annotation { "Feature Type Name" : "Feature", "Feature Type Description" : "" }
export const myFeature = defineFeature(function(context is Context, id is Id, definition is map)
    precondition{}
    {
        {
            var Q0;
            Q0=qCreatedBy(makeId("Top.planeOp"),FACE);
            var sketch = newSketch(context, id + "F0", { "sketchPlane" : qUnion([Q0])});
            skLineSegment(sketch, "E0.bottom", {"start": v(0, 0) * mm, "end": v(300, 0) * mm});
            skLineSegment(sketch, "E0.top", {"start": v(0, 148) * mm, "end": v(300, 148) * mm});
            skLineSegment(sketch, "E0.left", {"start": v(0, 0) * mm, "end": v(0, 148) * mm});
            skLineSegment(sketch, "E0.right", {"start": v(300, 0) * mm, "end": v(300, 148) * mm});
            skLineSegment(sketch, "E1.0", {"start": v(5, 143) * mm, "end": v(295, 143) * mm});
            skLineSegment(sketch, "E1.1", {"start": v(5, 5) * mm, "end": v(5, 143) * mm});
            skLineSegment(sketch, "E1.2", {"start": v(5, 5) * mm, "end": v(295, 5) * mm});
            skLineSegment(sketch, "E1.3", {"start": v(295, 5) * mm, "end": v(295, 143) * mm});
            skSolve(sketch);
        }
        {
            var Q0;
            Q0=qCreatedBy(makeId("Top.planeOp"),FACE);
            var sketch = newSketch(context, id + "F1", { "sketchPlane" : qUnion([Q0])});
            skLineSegment(sketch, "E2.bottom", {"start": v(159.6, 227.06) * mm, "end": v(245.86, 227.06) * mm});
            skLineSegment(sketch, "E2.top", {"start": v(159.6, 250.42) * mm, "end": v(245.86, 250.42) * mm});
            skLineSegment(sketch, "E2.left", {"start": v(159.6, 227.06) * mm, "end": v(159.6, 250.42) * mm});
            skLineSegment(sketch, "E2.right", {"start": v(245.86, 227.06) * mm, "end": v(245.86, 250.42) * mm});
            skLineSegment(sketch, "E3.bottom", {"start": v(5, 143) * mm, "end": v(295, 143) * mm, "construction": true});
            skLineSegment(sketch, "E3.top", {"start": v(5, 5) * mm, "end": v(295, 5) * mm, "construction": true});
            skLineSegment(sketch, "E3.left", {"start": v(5, 143) * mm, "end": v(5, 5) * mm, "construction": true});
            skLineSegment(sketch, "E3.right", {"start": v(295, 143) * mm, "end": v(295, 5) * mm, "construction": true});
            skLineSegment(sketch, "E4", {"start": v(5, 95) * mm, "end": v(295, 95) * mm, "construction": true});
            skLineSegment(sketch, "E5", {"start": v(5, 55) * mm, "end": v(295, 55) * mm, "construction": true});
            skLineSegment(sketch, "E6", {"start": v(5, 130) * mm, "end": v(295, 130) * mm, "construction": true});
            skLineSegment(sketch, "E7", {"start": v(5, 27) * mm, "end": v(295, 27) * mm, "construction": true});
            skLineSegment(sketch, "E8", {"start": v(5, 42) * mm, "end": v(295, 42) * mm, "construction": true});
            skLineSegment(sketch, "E9", {"start": v(295, 68) * mm, "end": v(5, 68) * mm, "construction": true});
            skSolve(sketch);
        }
        {
            var Q0;
            Q0=qCreatedBy(makeId("Top.planeOp"),FACE);
            var sketch = newSketch(context, id + "F2", { "sketchPlane" : qUnion([Q0])});
            skCircle(sketch, "E10", {"center": v(100, 130) * mm, "radius": 5 * mm});
            skCircle(sketch, "E11.1.0.0", {"center": v(125, 130) * mm, "radius": 5 * mm});
            skCircle(sketch, "E11.2.0.0", {"center": v(150, 130) * mm, "radius": 5 * mm});
            skCircle(sketch, "E11.3.0.0", {"center": v(175, 130) * mm, "radius": 5 * mm});
            skCircle(sketch, "E11.4.0.0", {"center": v(200, 130) * mm, "radius": 5 * mm});
            skCircle(sketch, "E11.5.0.0", {"center": v(225, 130) * mm, "radius": 5 * mm});
            skLineSegment(sketch, "E11.direction1", {"start": v(100, 130) * mm, "end": v(125, 130) * mm, "construction": true});
            skSolve(sketch);
        }
        {
            var Q0;
            Q0=qCreatedBy(makeId("Top.planeOp"),FACE);
            var sketch = newSketch(context, id + "F3", { "sketchPlane" : qUnion([Q0])});
            skCircle(sketch, "E12", {"center": v(35, 95) * mm, "radius": 15 * mm});
            skCircle(sketch, "E13.1.0.0", {"center": v(85, 95) * mm, "radius": 15 * mm});
            skCircle(sketch, "E13.2.0.0", {"center": v(135, 95) * mm, "radius": 15 * mm});
            skLineSegment(sketch, "E13.direction1", {"start": v(35, 95) * mm, "end": v(85, 95) * mm, "construction": true});
            skCircle(sketch, "E14", {"center": v(250, 95) * mm, "radius": 15 * mm});
            skSolve(sketch);
        }
        {
            var Q0;
            Q0=qCreatedBy(makeId("Top.planeOp"),FACE);
            var sketch = newSketch(context, id + "F4", { "sketchPlane" : qUnion([Q0])});
            skLineSegment(sketch, "E15.bottom", {"start": v(67.5, 35) * mm, "end": v(62.5, 35) * mm});
            skLineSegment(sketch, "E15.top", {"start": v(67.5, 19) * mm, "end": v(62.5, 19) * mm});
            skLineSegment(sketch, "E15.left", {"start": v(67.5, 35) * mm, "end": v(67.5, 19) * mm});
            skLineSegment(sketch, "E15.right", {"start": v(62.5, 35) * mm, "end": v(62.5, 19) * mm});
            skPoint(sketch, "E15.middle", {"position": v(65, 27) * mm});
            skLineSegment(sketch, "E16.1.0.0", {"start": v(78.5, 35) * mm, "end": v(78.5, 19) * mm});
            skLineSegment(sketch, "E16.1.0.1", {"start": v(83.5, 35) * mm, "end": v(78.5, 35) * mm});
            skLineSegment(sketch, "E16.1.0.2", {"start": v(83.5, 19) * mm, "end": v(78.5, 19) * mm});
            skLineSegment(sketch, "E16.1.0.3", {"start": v(83.5, 35) * mm, "end": v(83.5, 19) * mm});
            skLineSegment(sketch, "E16.2.0.0", {"start": v(94.5, 35) * mm, "end": v(94.5, 19) * mm});
            skLineSegment(sketch, "E16.2.0.1", {"start": v(99.5, 35) * mm, "end": v(94.5, 35) * mm});
            skLineSegment(sketch, "E16.2.0.2", {"start": v(99.5, 19) * mm, "end": v(94.5, 19) * mm});
            skLineSegment(sketch, "E16.2.0.3", {"start": v(99.5, 35) * mm, "end": v(99.5, 19) * mm});
            skLineSegment(sketch, "E16.3.0.0", {"start": v(110.5, 35) * mm, "end": v(110.5, 19) * mm});
            skLineSegment(sketch, "E16.3.0.1", {"start": v(115.5, 35) * mm, "end": v(110.5, 35) * mm});
            skLineSegment(sketch, "E16.3.0.2", {"start": v(115.5, 19) * mm, "end": v(110.5, 19) * mm});
            skLineSegment(sketch, "E16.3.0.3", {"start": v(115.5, 35) * mm, "end": v(115.5, 19) * mm});
            skLineSegment(sketch, "E16.4.0.0", {"start": v(126.5, 35) * mm, "end": v(126.5, 19) * mm});
            skLineSegment(sketch, "E16.4.0.1", {"start": v(131.5, 35) * mm, "end": v(126.5, 35) * mm});
            skLineSegment(sketch, "E16.4.0.2", {"start": v(131.5, 19) * mm, "end": v(126.5, 19) * mm});
            skLineSegment(sketch, "E16.4.0.3", {"start": v(131.5, 35) * mm, "end": v(131.5, 19) * mm});
            skLineSegment(sketch, "E16.5.0.0", {"start": v(142.5, 35) * mm, "end": v(142.5, 19) * mm});
            skLineSegment(sketch, "E16.5.0.1", {"start": v(147.5, 35) * mm, "end": v(142.5, 35) * mm});
            skLineSegment(sketch, "E16.5.0.2", {"start": v(147.5, 19) * mm, "end": v(142.5, 19) * mm});
            skLineSegment(sketch, "E16.5.0.3", {"start": v(147.5, 35) * mm, "end": v(147.5, 19) * mm});
            skLineSegment(sketch, "E16.6.0.0", {"start": v(158.5, 35) * mm, "end": v(158.5, 19) * mm});
            skLineSegment(sketch, "E16.6.0.1", {"start": v(163.5, 35) * mm, "end": v(158.5, 35) * mm});
            skLineSegment(sketch, "E16.6.0.2", {"start": v(163.5, 19) * mm, "end": v(158.5, 19) * mm});
            skLineSegment(sketch, "E16.6.0.3", {"start": v(163.5, 35) * mm, "end": v(163.5, 19) * mm});
            skLineSegment(sketch, "E16.7.0.0", {"start": v(174.5, 35) * mm, "end": v(174.5, 19) * mm});
            skLineSegment(sketch, "E16.7.0.1", {"start": v(179.5, 35) * mm, "end": v(174.5, 35) * mm});
            skLineSegment(sketch, "E16.7.0.2", {"start": v(179.5, 19) * mm, "end": v(174.5, 19) * mm});
            skLineSegment(sketch, "E16.7.0.3", {"start": v(179.5, 35) * mm, "end": v(179.5, 19) * mm});
            skLineSegment(sketch, "E16.8.0.0", {"start": v(190.5, 35) * mm, "end": v(190.5, 19) * mm});
            skLineSegment(sketch, "E16.8.0.1", {"start": v(195.5, 35) * mm, "end": v(190.5, 35) * mm});
            skLineSegment(sketch, "E16.8.0.2", {"start": v(195.5, 19) * mm, "end": v(190.5, 19) * mm});
            skLineSegment(sketch, "E16.8.0.3", {"start": v(195.5, 35) * mm, "end": v(195.5, 19) * mm});
            skLineSegment(sketch, "E16.9.0.0", {"start": v(206.5, 35) * mm, "end": v(206.5, 19) * mm});
            skLineSegment(sketch, "E16.9.0.1", {"start": v(211.5, 35) * mm, "end": v(206.5, 35) * mm});
            skLineSegment(sketch, "E16.9.0.2", {"start": v(211.5, 19) * mm, "end": v(206.5, 19) * mm});
            skLineSegment(sketch, "E16.9.0.3", {"start": v(211.5, 35) * mm, "end": v(211.5, 19) * mm});
            skLineSegment(sketch, "E16.direction1", {"start": v(62.5, 19) * mm, "end": v(78.5, 19) * mm, "construction": true});
            skLineSegment(sketch, "E17.0.10.0", {"start": v(222.5, 35) * mm, "end": v(222.5, 19) * mm});
            skLineSegment(sketch, "E17.3.10.0", {"start": v(227.5, 35) * mm, "end": v(222.5, 35) * mm});
            skLineSegment(sketch, "E17.6.10.0", {"start": v(227.5, 19) * mm, "end": v(222.5, 19) * mm});
            skLineSegment(sketch, "E17.9.10.0", {"start": v(227.5, 35) * mm, "end": v(227.5, 19) * mm});
            skLineSegment(sketch, "E17.0.11.0", {"start": v(238.5, 35) * mm, "end": v(238.5, 19) * mm});
            skLineSegment(sketch, "E17.3.11.0", {"start": v(243.5, 35) * mm, "end": v(238.5, 35) * mm});
            skLineSegment(sketch, "E17.6.11.0", {"start": v(243.5, 19) * mm, "end": v(238.5, 19) * mm});
            skLineSegment(sketch, "E17.9.11.0", {"start": v(243.5, 35) * mm, "end": v(243.5, 19) * mm});
            skLineSegment(sketch, "E18.bottom", {"start": v(124.5, 63) * mm, "end": v(119.5, 63) * mm});
            skLineSegment(sketch, "E18.top", {"start": v(124.5, 47) * mm, "end": v(119.5, 47) * mm});
            skLineSegment(sketch, "E18.left", {"start": v(124.5, 63) * mm, "end": v(124.5, 47) * mm});
            skLineSegment(sketch, "E18.right", {"start": v(119.5, 63) * mm, "end": v(119.5, 47) * mm});
            skPoint(sketch, "E18.middle", {"position": v(122, 55) * mm});
            skLineSegment(sketch, "E19.bottom", {"start": v(156.5, 63) * mm, "end": v(151.5, 63) * mm});
            skLineSegment(sketch, "E19.top", {"start": v(156.5, 47) * mm, "end": v(151.5, 47) * mm});
            skLineSegment(sketch, "E19.left", {"start": v(156.5, 63) * mm, "end": v(156.5, 47) * mm});
            skLineSegment(sketch, "E19.right", {"start": v(151.5, 63) * mm, "end": v(151.5, 47) * mm});
            skPoint(sketch, "E19.middle", {"position": v(154, 55) * mm});
            skLineSegment(sketch, "E20.bottom", {"start": v(140.5, 63) * mm, "end": v(135.5, 63) * mm});
            skLineSegment(sketch, "E20.top", {"start": v(140.5, 47) * mm, "end": v(135.5, 47) * mm});
            skLineSegment(sketch, "E20.left", {"start": v(140.5, 63) * mm, "end": v(140.5, 47) * mm});
            skLineSegment(sketch, "E20.right", {"start": v(135.5, 63) * mm, "end": v(135.5, 47) * mm});
            skPoint(sketch, "E20.middle", {"position": v(138, 55) * mm});
            skLineSegment(sketch, "E21.bottom", {"start": v(92.5, 63) * mm, "end": v(87.5, 63) * mm});
            skLineSegment(sketch, "E21.top", {"start": v(92.5, 47) * mm, "end": v(87.5, 47) * mm});
            skLineSegment(sketch, "E21.left", {"start": v(92.5, 63) * mm, "end": v(92.5, 47) * mm});
            skLineSegment(sketch, "E21.right", {"start": v(87.5, 63) * mm, "end": v(87.5, 47) * mm});
            skPoint(sketch, "E21.middle", {"position": v(90, 55) * mm});
            skLineSegment(sketch, "E22.bottom", {"start": v(76.5, 63) * mm, "end": v(71.5, 63) * mm});
            skLineSegment(sketch, "E22.top", {"start": v(76.5, 47) * mm, "end": v(71.5, 47) * mm});
            skLineSegment(sketch, "E22.left", {"start": v(76.5, 63) * mm, "end": v(76.5, 47) * mm});
            skLineSegment(sketch, "E22.right", {"start": v(71.5, 63) * mm, "end": v(71.5, 47) * mm});
            skPoint(sketch, "E22.middle", {"position": v(74, 55) * mm});
            skPoint(sketch, "E23", {"position": v(76.5, 55) * mm});
            skLineSegment(sketch, "E24.bottom", {"start": v(249, 57.5) * mm, "end": v(233, 57.5) * mm});
            skLineSegment(sketch, "E24.top", {"start": v(249, 52.5) * mm, "end": v(233, 52.5) * mm});
            skLineSegment(sketch, "E24.left", {"start": v(249, 57.5) * mm, "end": v(249, 52.5) * mm});
            skLineSegment(sketch, "E24.right", {"start": v(233, 57.5) * mm, "end": v(233, 52.5) * mm});
            skPoint(sketch, "E24.middle", {"position": v(241, 55) * mm});
            skLineSegment(sketch, "E25.bottom", {"start": v(283, 19) * mm, "end": v(263, 19) * mm});
            skLineSegment(sketch, "E25.top", {"start": v(283, 35) * mm, "end": v(263, 35) * mm});
            skLineSegment(sketch, "E25.left", {"start": v(283, 19) * mm, "end": v(283, 35) * mm});
            skLineSegment(sketch, "E25.right", {"start": v(263, 19) * mm, "end": v(263, 35) * mm});
            skPoint(sketch, "E25.middle", {"position": v(273, 27) * mm});
            skLineSegment(sketch, "E26.bottom", {"start": v(35, 19) * mm, "end": v(15, 19) * mm});
            skLineSegment(sketch, "E26.top", {"start": v(35, 35) * mm, "end": v(15, 35) * mm});
            skLineSegment(sketch, "E26.left", {"start": v(35, 19) * mm, "end": v(35, 35) * mm});
            skLineSegment(sketch, "E26.right", {"start": v(15, 19) * mm, "end": v(15, 35) * mm});
            skPoint(sketch, "E26.middle", {"position": v(25, 27) * mm});
            skPoint(sketch, "E27", {"position": v(83.5, 27) * mm});
            skPoint(sketch, "E28", {"position": v(241, 35) * mm});
            skLineSegment(sketch, "E29.bottom", {"start": v(281, 60) * mm, "end": v(265, 60) * mm});
            skLineSegment(sketch, "E29.top", {"start": v(281, 55) * mm, "end": v(265, 55) * mm});
            skLineSegment(sketch, "E29.left", {"start": v(281, 60) * mm, "end": v(281, 55) * mm});
            skLineSegment(sketch, "E29.right", {"start": v(265, 60) * mm, "end": v(265, 55) * mm});
            skPoint(sketch, "E29.middle", {"position": v(273, 57.5) * mm});
            skPoint(sketch, "E30", {"position": v(273, 35) * mm});
            skLineSegment(sketch, "E31.bottom", {"start": v(33, 57.5) * mm, "end": v(17, 57.5) * mm});
            skLineSegment(sketch, "E31.top", {"start": v(33, 52.5) * mm, "end": v(17, 52.5) * mm});
            skLineSegment(sketch, "E31.left", {"start": v(33, 57.5) * mm, "end": v(33, 52.5) * mm});
            skLineSegment(sketch, "E31.right", {"start": v(17, 57.5) * mm, "end": v(17, 52.5) * mm});
            skPoint(sketch, "E31.middle", {"position": v(25, 55) * mm});
            skLineSegment(sketch, "E32.bottom", {"start": v(47.5, 19) * mm, "end": v(42.5, 19) * mm});
            skLineSegment(sketch, "E32.top", {"start": v(47.5, 35) * mm, "end": v(42.5, 35) * mm});
            skLineSegment(sketch, "E32.left", {"start": v(47.5, 19) * mm, "end": v(47.5, 35) * mm});
            skLineSegment(sketch, "E32.right", {"start": v(42.5, 19) * mm, "end": v(42.5, 35) * mm});
            skPoint(sketch, "E32.middle", {"position": v(45, 27) * mm});
            skCircle(sketch, "E33", {"center": v(145, 42) * mm, "radius": 1.5 * mm});
            skCircle(sketch, "E34", {"center": v(161, 42) * mm, "radius": 1.5 * mm});
            skCircle(sketch, "E35", {"center": v(129, 42) * mm, "radius": 1.5 * mm});
            skCircle(sketch, "E36", {"center": v(113, 42) * mm, "radius": 1.5 * mm});
            skCircle(sketch, "E37", {"center": v(74, 68) * mm, "radius": 1.5 * mm});
            skCircle(sketch, "E38", {"center": v(90, 68) * mm, "radius": 1.5 * mm});
            skCircle(sketch, "E39", {"center": v(97, 42) * mm, "radius": 1.5 * mm});
            skCircle(sketch, "E40", {"center": v(81, 42) * mm, "radius": 1.5 * mm});
            skCircle(sketch, "E41", {"center": v(65, 42) * mm, "radius": 1.5 * mm});
            skPoint(sketch, "E42", {"position": v(65, 35) * mm});
            skPoint(sketch, "E43", {"position": v(81, 35) * mm});
            skPoint(sketch, "E44", {"position": v(97, 35) * mm});
            skPoint(sketch, "E45", {"position": v(113, 35) * mm});
            skPoint(sketch, "E46", {"position": v(129, 35) * mm});
            skPoint(sketch, "E47", {"position": v(145, 35) * mm});
            skPoint(sketch, "E48", {"position": v(161, 35) * mm});
            skCircle(sketch, "E49", {"center": v(209, 42) * mm, "radius": 1.5 * mm});
            skCircle(sketch, "E50", {"center": v(225, 42) * mm, "radius": 1.5 * mm});
            skCircle(sketch, "E51", {"center": v(154, 68) * mm, "radius": 1.5 * mm});
            skCircle(sketch, "E52", {"center": v(138, 68) * mm, "radius": 1.5 * mm});
            skCircle(sketch, "E53", {"center": v(217, 68) * mm, "radius": 1.5 * mm});
            skCircle(sketch, "E54", {"center": v(122, 68) * mm, "radius": 1.5 * mm});
            skCircle(sketch, "E55", {"center": v(177, 42) * mm, "radius": 1.5 * mm});
            skCircle(sketch, "E56", {"center": v(193, 42) * mm, "radius": 1.5 * mm});
            skPoint(sketch, "E57", {"position": v(122, 63) * mm});
            skPoint(sketch, "E58", {"position": v(138, 63) * mm});
            skPoint(sketch, "E59", {"position": v(154, 63) * mm});
            skPoint(sketch, "E60", {"position": v(177, 35) * mm});
            skPoint(sketch, "E61", {"position": v(193, 35) * mm});
            skPoint(sketch, "E62", {"position": v(209, 35) * mm});
            skPoint(sketch, "E63", {"position": v(225, 35) * mm});
            skCircle(sketch, "E64", {"center": v(25, 42) * mm, "radius": 1.5 * mm});
            skPoint(sketch, "E65", {"position": v(25, 35) * mm});
            skLineSegment(sketch, "E66.bottom", {"start": v(47.5, 52.5) * mm, "end": v(63.5, 52.5) * mm});
            skLineSegment(sketch, "E66.top", {"start": v(47.5, 57.5) * mm, "end": v(63.5, 57.5) * mm});
            skLineSegment(sketch, "E66.left", {"start": v(47.5, 52.5) * mm, "end": v(47.5, 57.5) * mm});
            skLineSegment(sketch, "E66.right", {"start": v(63.5, 52.5) * mm, "end": v(63.5, 57.5) * mm});
            skCircle(sketch, "E67", {"center": v(55.5, 68) * mm, "radius": 1.5 * mm});
            skPoint(sketch, "E67.centerSnap0", {"position": v(55.5, 57.5) * mm});
            skSolve(sketch);
        }
        {
            var Q0;
            Q0=qCreatedBy(makeId("Top.planeOp"),FACE);
            var sketch = newSketch(context, id + "F5", { "sketchPlane" : qUnion([Q0])});
            skText(sketch, "E68", { "text": "TB 303", "fontName": "OpenSans-Regular.ttf"});
            skPoint(sketch, "E69", {"position": v(197.71, 95) * mm});
            skText(sketch, "E70", { "text": "Compueter Controled\n", "fontName": "OpenSans-Regular.ttf"});
            skLineSegment(sketch, "E71", {"start": v(215.4, 87) * mm, "end": v(215.4, 91) * mm, "construction": true});
            skText(sketch, "E72", { "text": "Roland", "fontName": "OpenSans-Regular.ttf"});
            skText(sketch, "E73", { "text": "Bass line", "fontName": "OpenSans-Regular.ttf"});
            const initialGuessF5  = {"E68": [0.18003, 0.091, 1, 0, 0.008], "E70": [0.15897, 0.083, 1, 0, 0.004], "E72": [0.029, 0.124, 1, 0, 0.01], "E73": [0.23932, 0.124, 1, 0, 0.008]};
            skSetInitialGuess(sketch, initialGuessF5);
            skSolve(sketch);
        }
        {
            var Q0;
            Q0=makeQuery(id+"F0.imprint","IMPRINT",FACE,{"disambiguationData":[TD([[makeQuery(id+"F0.imprint","IMPRINT",EDGE,{"derivedFrom":sQuery(id+"F0.wireOp",EDGE,"E1.0")}),-1.0]])]});
            extrude(context, id + "F6", {"entities" : qUnion([Q0]), "depth" : 55 * mm, "hasSecondDirection" : true, "secondDirectionOppositeDirection" : false, "secondDirectionDepth" : 50 * mm});
        }
        {
            var Q0;
            Q0=makeQuery(id+"F4.imprint","IMPRINT",FACE,{"disambiguationData":[TD([[makeQuery(id+"F4.imprint","IMPRINT",EDGE,{"derivedFrom":sQuery(id+"F4.wireOp",EDGE,"E16.6.0.0")}),1.0]])]});
            var Q1;
            Q1=makeQuery(id+"F4.imprint","IMPRINT",FACE,{"disambiguationData":[TD([[makeQuery(id+"F4.imprint","IMPRINT",EDGE,{"derivedFrom":sQuery(id+"F4.wireOp",EDGE,"E16.2.0.0")}),1.0]])]});
            var Q2;
            Q2=makeQuery(id+"F4.imprint","IMPRINT",FACE,{"disambiguationData":[TD([[makeQuery(id+"F4.imprint","IMPRINT",EDGE,{"derivedFrom":sQuery(id+"F4.wireOp",EDGE,"E17.0.11.0")}),1.0]])]});
            var Q3;
            Q3=makeQuery(id+"F4.imprint","IMPRINT",FACE,{"disambiguationData":[TD([[makeQuery(id+"F4.imprint","IMPRINT",EDGE,{"derivedFrom":sQuery(id+"F4.wireOp",EDGE,"E16.4.0.0")}),1.0]])]});
            var Q4;
            Q4=makeQuery(id+"F3.imprint","IMPRINT",FACE,{"disambiguationData":[TD([[makeQuery(id+"F3.imprint","IMPRINT",EDGE,{"derivedFrom":sQuery(id+"F3.wireOp",EDGE,"E14")}),1.0]])]});
            var Q5;
            Q5=makeQuery(id+"F4.imprint","IMPRINT",FACE,{"disambiguationData":[TD([[makeQuery(id+"F4.imprint","IMPRINT",EDGE,{"derivedFrom":sQuery(id+"F4.wireOp",EDGE,"E16.3.0.0")}),1.0]])]});
            var Q6;
            Q6=makeQuery(id+"F4.imprint","IMPRINT",FACE,{"disambiguationData":[TD([[makeQuery(id+"F4.imprint","IMPRINT",EDGE,{"derivedFrom":sQuery(id+"F4.wireOp",EDGE,"E16.5.0.0")}),1.0]])]});
            var Q7;
            Q7=makeQuery(id+"F4.imprint","IMPRINT",FACE,{"disambiguationData":[TD([[makeQuery(id+"F4.imprint","IMPRINT",EDGE,{"derivedFrom":sQuery(id+"F4.wireOp",EDGE,"E16.7.0.0")}),1.0]])]});
            var Q8;
            Q8=makeQuery(id+"F3.imprint","IMPRINT",FACE,{"disambiguationData":[TD([[makeQuery(id+"F3.imprint","IMPRINT",EDGE,{"derivedFrom":sQuery(id+"F3.wireOp",EDGE,"E13.1.0.0")}),1.0]])]});
            var Q9;
            Q9=makeQuery(id+"F4.imprint","IMPRINT",FACE,{"disambiguationData":[TD([[makeQuery(id+"F4.imprint","IMPRINT",EDGE,{"derivedFrom":sQuery(id+"F4.wireOp",EDGE,"E17.0.10.0")}),1.0]])]});
            var Q10;
            Q10=makeQuery(id+"F4.imprint","IMPRINT",FACE,{"disambiguationData":[TD([[makeQuery(id+"F4.imprint","IMPRINT",EDGE,{"derivedFrom":sQuery(id+"F4.wireOp",EDGE,"E26.bottom")}),-1.0]])]});
            var Q11;
            Q11=makeQuery(id+"F4.imprint","IMPRINT",FACE,{"disambiguationData":[TD([[makeQuery(id+"F4.imprint","IMPRINT",EDGE,{"derivedFrom":sQuery(id+"F4.wireOp",EDGE,"E25.bottom")}),-1.0]])]});
            var Q12;
            Q12=makeQuery(id+"F3.imprint","IMPRINT",FACE,{"disambiguationData":[TD([[makeQuery(id+"F3.imprint","IMPRINT",EDGE,{"derivedFrom":sQuery(id+"F3.wireOp",EDGE,"E12")}),1.0]])]});
            var Q13;
            Q13=makeQuery(id+"F4.imprint","IMPRINT",FACE,{"disambiguationData":[TD([[makeQuery(id+"F4.imprint","IMPRINT",EDGE,{"derivedFrom":sQuery(id+"F4.wireOp",EDGE,"E16.9.0.0")}),1.0]])]});
            var Q14;
            Q14=makeQuery(id+"F3.imprint","IMPRINT",FACE,{"disambiguationData":[TD([[makeQuery(id+"F3.imprint","IMPRINT",EDGE,{"derivedFrom":sQuery(id+"F3.wireOp",EDGE,"E13.2.0.0")}),1.0]])]});
            var Q15;
            Q15=makeQuery(id+"F4.imprint","IMPRINT",FACE,{"disambiguationData":[TD([[makeQuery(id+"F4.imprint","IMPRINT",EDGE,{"derivedFrom":sQuery(id+"F4.wireOp",EDGE,"E16.8.0.0")}),1.0]])]});
            var Q16;
            Q16=makeQuery(id+"F4.imprint","IMPRINT",FACE,{"disambiguationData":[TD([[makeQuery(id+"F4.imprint","IMPRINT",EDGE,{"derivedFrom":sQuery(id+"F4.wireOp",EDGE,"E29.bottom")}),1.0]])]});
            var Q17;
            Q17=makeQuery(id+"F4.imprint","IMPRINT",FACE,{"disambiguationData":[TD([[makeQuery(id+"F4.imprint","IMPRINT",EDGE,{"derivedFrom":sQuery(id+"F4.wireOp",EDGE,"MlsZsGtn-eIpS-iZ8F-oq2x-HGk03Y0HB9p6.bottom")}),1.0]])]});
            var Q18;
            Q18=makeQuery(id+"F4.imprint","IMPRINT",FACE,{"disambiguationData":[TD([[makeQuery(id+"F4.imprint","IMPRINT",EDGE,{"derivedFrom":sQuery(id+"F4.wireOp",EDGE,"E24.bottom")}),1.0]])]});
            var Q19;
            Q19=makeQuery(id+"F4.imprint","IMPRINT",FACE,{"disambiguationData":[TD([[makeQuery(id+"F4.imprint","IMPRINT",EDGE,{"derivedFrom":sQuery(id+"F4.wireOp",EDGE,"E15.bottom")}),1.0]])]});
            var Q20;
            Q20=makeQuery(id+"F4.imprint","IMPRINT",FACE,{"disambiguationData":[TD([[makeQuery(id+"F4.imprint","IMPRINT",EDGE,{"derivedFrom":sQuery(id+"F4.wireOp",EDGE,"E16.1.0.0")}),1.0]])]});
            var Q21;
            Q21=makeQuery(id+"F2.imprint","IMPRINT",FACE,{"disambiguationData":[TD([[makeQuery(id+"F2.imprint","IMPRINT",EDGE,{"derivedFrom":sQuery(id+"F2.wireOp",EDGE,"E11.4.0.0")}),1.0]])]});
            var Q22;
            Q22=makeQuery(id+"F2.imprint","IMPRINT",FACE,{"disambiguationData":[TD([[makeQuery(id+"F2.imprint","IMPRINT",EDGE,{"derivedFrom":sQuery(id+"F2.wireOp",EDGE,"E11.3.0.0")}),1.0]])]});
            var Q23;
            Q23=makeQuery(id+"F4.imprint","IMPRINT",FACE,{"disambiguationData":[TD([[makeQuery(id+"F4.imprint","IMPRINT",EDGE,{"derivedFrom":sQuery(id+"F4.wireOp",EDGE,"E20.bottom")}),1.0]])]});
            var Q24;
            Q24=makeQuery(id+"F4.imprint","IMPRINT",FACE,{"disambiguationData":[TD([[makeQuery(id+"F4.imprint","IMPRINT",EDGE,{"derivedFrom":sQuery(id+"F4.wireOp",EDGE,"E21.bottom")}),1.0]])]});
            var Q25;
            Q25=makeQuery(id+"F4.imprint","IMPRINT",FACE,{"disambiguationData":[TD([[makeQuery(id+"F4.imprint","IMPRINT",EDGE,{"derivedFrom":sQuery(id+"F4.wireOp",EDGE,"E22.bottom")}),1.0]])]});
            var Q26;
            Q26=makeQuery(id+"F4.imprint","IMPRINT",FACE,{"disambiguationData":[TD([[makeQuery(id+"F4.imprint","IMPRINT",EDGE,{"derivedFrom":sQuery(id+"F4.wireOp",EDGE,"E32.bottom")}),-1.0]])]});
            var Q27;
            Q27=makeQuery(id+"F2.imprint","IMPRINT",FACE,{"disambiguationData":[TD([[makeQuery(id+"F2.imprint","IMPRINT",EDGE,{"derivedFrom":sQuery(id+"F2.wireOp",EDGE,"E11.2.0.0")}),1.0]])]});
            var Q28;
            Q28=makeQuery(id+"F2.imprint","IMPRINT",FACE,{"disambiguationData":[TD([[makeQuery(id+"F2.imprint","IMPRINT",EDGE,{"derivedFrom":sQuery(id+"F2.wireOp",EDGE,"E10")}),1.0]])]});
            var Q29;
            Q29=makeQuery(id+"F4.imprint","IMPRINT",FACE,{"disambiguationData":[TD([[makeQuery(id+"F4.imprint","IMPRINT",EDGE,{"derivedFrom":sQuery(id+"F4.wireOp",EDGE,"E31.bottom")}),1.0]])]});
            var Q30;
            Q30=makeQuery(id+"F4.imprint","IMPRINT",FACE,{"disambiguationData":[TD([[makeQuery(id+"F4.imprint","IMPRINT",EDGE,{"derivedFrom":sQuery(id+"F4.wireOp",EDGE,"E19.bottom")}),1.0]])]});
            var Q31;
            Q31=makeQuery(id+"F2.imprint","IMPRINT",FACE,{"disambiguationData":[TD([[makeQuery(id+"F2.imprint","IMPRINT",EDGE,{"derivedFrom":sQuery(id+"F2.wireOp",EDGE,"E11.1.0.0")}),1.0]])]});
            var Q32;
            Q32=makeQuery(id+"F4.imprint","IMPRINT",FACE,{"disambiguationData":[TD([[makeQuery(id+"F4.imprint","IMPRINT",EDGE,{"derivedFrom":sQuery(id+"F4.wireOp",EDGE,"E18.bottom")}),1.0]])]});
            var Q33;
            Q33=makeQuery(id+"F2.imprint","IMPRINT",FACE,{"disambiguationData":[TD([[makeQuery(id+"F2.imprint","IMPRINT",EDGE,{"derivedFrom":sQuery(id+"F2.wireOp",EDGE,"E11.5.0.0")}),1.0]])]});
            var Q34;
            Q34=makeQuery(id+"F4.imprint","IMPRINT",FACE,{"disambiguationData":[TD([[makeQuery(id+"F4.imprint","IMPRINT",EDGE,{"derivedFrom":sQuery(id+"F4.wireOp",EDGE,"E53")}),1.0]])]});
            var Q35;
            Q35=makeQuery(id+"F4.imprint","IMPRINT",FACE,{"disambiguationData":[TD([[makeQuery(id+"F4.imprint","IMPRINT",EDGE,{"derivedFrom":sQuery(id+"F4.wireOp",EDGE,"E50")}),1.0]])]});
            var Q36;
            Q36=makeQuery(id+"F4.imprint","IMPRINT",FACE,{"disambiguationData":[TD([[makeQuery(id+"F4.imprint","IMPRINT",EDGE,{"derivedFrom":sQuery(id+"F4.wireOp",EDGE,"E49")}),1.0]])]});
            var Q37;
            Q37=makeQuery(id+"F4.imprint","IMPRINT",FACE,{"disambiguationData":[TD([[makeQuery(id+"F4.imprint","IMPRINT",EDGE,{"derivedFrom":sQuery(id+"F4.wireOp",EDGE,"E35")}),1.0]])]});
            var Q38;
            Q38=makeQuery(id+"F4.imprint","IMPRINT",FACE,{"disambiguationData":[TD([[makeQuery(id+"F4.imprint","IMPRINT",EDGE,{"derivedFrom":sQuery(id+"F4.wireOp",EDGE,"E34")}),1.0]])]});
            var Q39;
            Q39=makeQuery(id+"F4.imprint","IMPRINT",FACE,{"disambiguationData":[TD([[makeQuery(id+"F4.imprint","IMPRINT",EDGE,{"derivedFrom":sQuery(id+"F4.wireOp",EDGE,"3ac610bb-b30e-4773-8843-c200d17e3087")}),1.0]])]});
            var Q40;
            Q40=makeQuery(id+"F4.imprint","IMPRINT",FACE,{"disambiguationData":[TD([[makeQuery(id+"F4.imprint","IMPRINT",EDGE,{"derivedFrom":sQuery(id+"F4.wireOp",EDGE,"E55")}),1.0]])]});
            var Q41;
            Q41=makeQuery(id+"F4.imprint","IMPRINT",FACE,{"disambiguationData":[TD([[makeQuery(id+"F4.imprint","IMPRINT",EDGE,{"derivedFrom":sQuery(id+"F4.wireOp",EDGE,"E33")}),1.0]])]});
            var Q42;
            Q42=makeQuery(id+"F4.imprint","IMPRINT",FACE,{"disambiguationData":[TD([[makeQuery(id+"F4.imprint","IMPRINT",EDGE,{"derivedFrom":sQuery(id+"F4.wireOp",EDGE,"E64")}),1.0]])]});
            var Q43;
            Q43=makeQuery(id+"F4.imprint","IMPRINT",FACE,{"disambiguationData":[TD([[makeQuery(id+"F4.imprint","IMPRINT",EDGE,{"derivedFrom":sQuery(id+"F4.wireOp",EDGE,"E36")}),1.0]])]});
            var Q44;
            Q44=makeQuery(id+"F4.imprint","IMPRINT",FACE,{"disambiguationData":[TD([[makeQuery(id+"F4.imprint","IMPRINT",EDGE,{"derivedFrom":sQuery(id+"F4.wireOp",EDGE,"E40")}),1.0]])]});
            var Q45;
            Q45=makeQuery(id+"F4.imprint","IMPRINT",FACE,{"disambiguationData":[TD([[makeQuery(id+"F4.imprint","IMPRINT",EDGE,{"derivedFrom":sQuery(id+"F4.wireOp",EDGE,"E54")}),1.0]])]});
            var Q46;
            Q46=makeQuery(id+"F4.imprint","IMPRINT",FACE,{"disambiguationData":[TD([[makeQuery(id+"F4.imprint","IMPRINT",EDGE,{"derivedFrom":sQuery(id+"F4.wireOp",EDGE,"E52")}),1.0]])]});
            var Q47;
            Q47=makeQuery(id+"F4.imprint","IMPRINT",FACE,{"disambiguationData":[TD([[makeQuery(id+"F4.imprint","IMPRINT",EDGE,{"derivedFrom":sQuery(id+"F4.wireOp",EDGE,"E37")}),1.0]])]});
            var Q48;
            Q48=makeQuery(id+"F4.imprint","IMPRINT",FACE,{"disambiguationData":[TD([[makeQuery(id+"F4.imprint","IMPRINT",EDGE,{"derivedFrom":sQuery(id+"F4.wireOp",EDGE,"E41")}),1.0]])]});
            var Q49;
            Q49=makeQuery(id+"F4.imprint","IMPRINT",FACE,{"disambiguationData":[TD([[makeQuery(id+"F4.imprint","IMPRINT",EDGE,{"derivedFrom":sQuery(id+"F4.wireOp",EDGE,"E38")}),1.0]])]});
            var Q50;
            Q50=makeQuery(id+"F4.imprint","IMPRINT",FACE,{"disambiguationData":[TD([[makeQuery(id+"F4.imprint","IMPRINT",EDGE,{"derivedFrom":sQuery(id+"F4.wireOp",EDGE,"E56")}),1.0]])]});
            var Q51;
            Q51=makeQuery(id+"F4.imprint","IMPRINT",FACE,{"disambiguationData":[TD([[makeQuery(id+"F4.imprint","IMPRINT",EDGE,{"derivedFrom":sQuery(id+"F4.wireOp",EDGE,"aac88f0d-ab9e-401a-b35d-e5a6f0b392a7")}),1.0]])]});
            var Q52;
            Q52=makeQuery(id+"F4.imprint","IMPRINT",FACE,{"disambiguationData":[TD([[makeQuery(id+"F4.imprint","IMPRINT",EDGE,{"derivedFrom":sQuery(id+"F4.wireOp",EDGE,"E39")}),1.0]])]});
            var Q53;
            Q53=makeQuery(id+"F4.imprint","IMPRINT",FACE,{"disambiguationData":[TD([[makeQuery(id+"F4.imprint","IMPRINT",EDGE,{"derivedFrom":sQuery(id+"F4.wireOp",EDGE,"E51")}),1.0]])]});
            var Q54;
            Q54=makeQuery(id+"F4.imprint","IMPRINT",FACE,{"disambiguationData":[TD([[makeQuery(id+"F4.imprint","IMPRINT",EDGE,{"derivedFrom":sQuery(id+"F4.wireOp",EDGE,"E66.bottom")}),1.0]])]});
            var Q55;
            Q55=makeQuery(id+"F4.imprint","IMPRINT",FACE,{"disambiguationData":[TD([[makeQuery(id+"F4.imprint","IMPRINT",EDGE,{"derivedFrom":sQuery(id+"F4.wireOp",EDGE,"E67")}),1.0]])]});
            extrude(context, id + "F7", {"entities" : qUnion([Q0, Q1, Q2, Q3, Q4, Q5, Q6, Q7, Q8, Q9, Q10, Q11, Q12, Q13, Q14, Q15, Q16, Q17, Q18, Q19, Q20, Q21, Q22, Q23, Q24, Q25, Q26, Q27, Q28, Q29, Q30, Q31, Q32, Q33, Q34, Q35, Q36, Q37, Q38, Q39, Q40, Q41, Q42, Q43, Q44, Q45, Q46, Q47, Q48, Q49, Q50, Q51, Q52, Q53, Q54, Q55]), "operationType" : NewBodyOperationType.REMOVE, "depth" : 55 * mm, "hasSecondDirection" : true, "secondDirectionOppositeDirection" : false, "secondDirectionDepth" : 50 * mm});
        }
        {
            var Q0;
            Q0=makeQuery(id+"F0.imprint","IMPRINT",FACE,{"disambiguationData":[TD([[makeQuery(id+"F0.imprint","IMPRINT",EDGE,{"derivedFrom":sQuery(id+"F0.wireOp",EDGE,"E0.bottom")}),1.0]])]});
            extrude(context, id + "F8", {"entities" : qUnion([Q0]), "operationType" : NewBodyOperationType.ADD, "depth" : 52 * mm});
        }
        {
            var Q0;
            Q0=makeQuery(id+"F5.imprint","IMPRINT",FACE,{"disambiguationData":[TD([[makeQuery(id+"F5.imprint","IMPRINT",EDGE,{"derivedFrom":sQuery(id+"F5.wireOp",EDGE,"E68.sketch_text.stroke-61")}),-1.0]])]});
            var Q1;
            Q1=makeQuery(id+"F5.imprint","IMPRINT",FACE,{"disambiguationData":[TD([[makeQuery(id+"F5.imprint","IMPRINT",EDGE,{"derivedFrom":sQuery(id+"F5.wireOp",EDGE,"E68.sketch_text.stroke-77")}),-1.0]])]});
            var Q2;
            Q2=makeQuery(id+"F5.imprint","IMPRINT",FACE,{"disambiguationData":[TD([[makeQuery(id+"F5.imprint","IMPRINT",EDGE,{"derivedFrom":sQuery(id+"F5.wireOp",EDGE,"E68.sketch_text.stroke-33")}),-1.0]])]});
            var Q3;
            Q3=makeQuery(id+"F5.imprint","IMPRINT",FACE,{"disambiguationData":[TD([[makeQuery(id+"F5.imprint","IMPRINT",EDGE,{"derivedFrom":sQuery(id+"F5.wireOp",EDGE,"E68.sketch_text.stroke-8")}),-1.0]])]});
            var Q4;
            Q4=makeQuery(id+"F5.imprint","IMPRINT",FACE,{"disambiguationData":[TD([[makeQuery(id+"F5.imprint","IMPRINT",EDGE,{"derivedFrom":sQuery(id+"F5.wireOp",EDGE,"E68.sketch_text.stroke-0")}),-1.0]])]});
            extrude(context, id + "F9", {"entities" : qUnion([Q0, Q1, Q2, Q3, Q4]), "operationType" : NewBodyOperationType.ADD, "depth" : 56 * mm, "hasSecondDirection" : true, "secondDirectionOppositeDirection" : false, "secondDirectionDepth" : 55 * mm});
        }
        {
            var Q0;
            Q0=makeQuery(id+"F5.imprint","IMPRINT",FACE,{"disambiguationData":[TD([[makeQuery(id+"F5.imprint","IMPRINT",EDGE,{"derivedFrom":sQuery(id+"F5.wireOp",EDGE,"E70.sketch_text.stroke-85")}),-1.0]])]});
            var Q1;
            Q1=makeQuery(id+"F5.imprint","IMPRINT",FACE,{"disambiguationData":[TD([[makeQuery(id+"F5.imprint","IMPRINT",EDGE,{"derivedFrom":sQuery(id+"F5.wireOp",EDGE,"E70.sketch_text.stroke-102")}),-1.0]])]});
            var Q2;
            Q2=makeQuery(id+"F5.imprint","IMPRINT",FACE,{"disambiguationData":[TD([[makeQuery(id+"F5.imprint","IMPRINT",EDGE,{"derivedFrom":sQuery(id+"F5.wireOp",EDGE,"E70.sketch_text.stroke-121")}),-1.0]])]});
            var Q3;
            Q3=makeQuery(id+"F5.imprint","IMPRINT",FACE,{"disambiguationData":[TD([[makeQuery(id+"F5.imprint","IMPRINT",EDGE,{"derivedFrom":sQuery(id+"F5.wireOp",EDGE,"E70.sketch_text.stroke-60")}),-1.0]])]});
            var Q4;
            Q4=makeQuery(id+"F5.imprint","IMPRINT",FACE,{"disambiguationData":[TD([[makeQuery(id+"F5.imprint","IMPRINT",EDGE,{"derivedFrom":sQuery(id+"F5.wireOp",EDGE,"E70.sketch_text.stroke-32")}),-1.0]])]});
            var Q5;
            Q5=makeQuery(id+"F5.imprint","IMPRINT",FACE,{"disambiguationData":[TD([[makeQuery(id+"F5.imprint","IMPRINT",EDGE,{"derivedFrom":sQuery(id+"F5.wireOp",EDGE,"E70.sketch_text.stroke-140")}),-1.0]])]});
            var Q6;
            Q6=makeQuery(id+"F5.imprint","IMPRINT",FACE,{"disambiguationData":[TD([[makeQuery(id+"F5.imprint","IMPRINT",EDGE,{"derivedFrom":sQuery(id+"F5.wireOp",EDGE,"E70.sketch_text.stroke-159")}),-1.0]])]});
            var Q7;
            Q7=makeQuery(id+"F5.imprint","IMPRINT",FACE,{"disambiguationData":[TD([[makeQuery(id+"F5.imprint","IMPRINT",EDGE,{"derivedFrom":sQuery(id+"F5.wireOp",EDGE,"E70.sketch_text.stroke-172")}),-1.0]])]});
            var Q8;
            Q8=makeQuery(id+"F5.imprint","IMPRINT",FACE,{"disambiguationData":[TD([[makeQuery(id+"F5.imprint","IMPRINT",EDGE,{"derivedFrom":sQuery(id+"F5.wireOp",EDGE,"E70.sketch_text.stroke-187")}),-1.0]])]});
            var Q9;
            Q9=makeQuery(id+"F5.imprint","IMPRINT",FACE,{"disambiguationData":[TD([[makeQuery(id+"F5.imprint","IMPRINT",EDGE,{"derivedFrom":sQuery(id+"F5.wireOp",EDGE,"E70.sketch_text.stroke-221")}),-1.0]])]});
            var Q10;
            Q10=makeQuery(id+"F5.imprint","IMPRINT",FACE,{"disambiguationData":[TD([[makeQuery(id+"F5.imprint","IMPRINT",EDGE,{"derivedFrom":sQuery(id+"F5.wireOp",EDGE,"E70.sketch_text.stroke-240")}),-1.0]])]});
            var Q11;
            Q11=makeQuery(id+"F5.imprint","IMPRINT",FACE,{"disambiguationData":[TD([[makeQuery(id+"F5.imprint","IMPRINT",EDGE,{"derivedFrom":sQuery(id+"F5.wireOp",EDGE,"E70.sketch_text.stroke-204")}),-1.0]])]});
            var Q12;
            Q12=makeQuery(id+"F5.imprint","IMPRINT",FACE,{"disambiguationData":[TD([[makeQuery(id+"F5.imprint","IMPRINT",EDGE,{"derivedFrom":sQuery(id+"F5.wireOp",EDGE,"E70.sketch_text.stroke-253")}),-1.0]])]});
            var Q13;
            Q13=makeQuery(id+"F5.imprint","IMPRINT",FACE,{"disambiguationData":[TD([[makeQuery(id+"F5.imprint","IMPRINT",EDGE,{"derivedFrom":sQuery(id+"F5.wireOp",EDGE,"E70.sketch_text.stroke-270")}),-1.0]])]});
            var Q14;
            Q14=makeQuery(id+"F5.imprint","IMPRINT",FACE,{"disambiguationData":[TD([[makeQuery(id+"F5.imprint","IMPRINT",EDGE,{"derivedFrom":sQuery(id+"F5.wireOp",EDGE,"E70.sketch_text.stroke-274")}),-1.0]])]});
            var Q15;
            Q15=makeQuery(id+"F5.imprint","IMPRINT",FACE,{"disambiguationData":[TD([[makeQuery(id+"F5.imprint","IMPRINT",EDGE,{"derivedFrom":sQuery(id+"F5.wireOp",EDGE,"E70.sketch_text.stroke-293")}),-1.0]])]});
            var Q16;
            Q16=makeQuery(id+"F5.imprint","IMPRINT",FACE,{"disambiguationData":[TD([[makeQuery(id+"F5.imprint","IMPRINT",EDGE,{"derivedFrom":sQuery(id+"F5.wireOp",EDGE,"E70.sketch_text.stroke-0")}),-1.0]])]});
            var Q17;
            Q17=makeQuery(id+"F5.imprint","IMPRINT",FACE,{"disambiguationData":[TD([[makeQuery(id+"F5.imprint","IMPRINT",EDGE,{"derivedFrom":sQuery(id+"F5.wireOp",EDGE,"E70.sketch_text.stroke-15")}),-1.0]])]});
            extrude(context, id + "F10", {"entities" : qUnion([Q0, Q1, Q2, Q3, Q4, Q5, Q6, Q7, Q8, Q9, Q10, Q11, Q12, Q13, Q14, Q15, Q16, Q17]), "operationType" : NewBodyOperationType.ADD, "depth" : 56 * mm, "hasSecondDirection" : true, "secondDirectionOppositeDirection" : false, "secondDirectionDepth" : 55 * mm});
        }
        {
            var Q0;
            Q0=makeQuery(id+"F5.imprint","IMPRINT",FACE,{"disambiguationData":[TD([[makeQuery(id+"F5.imprint","IMPRINT",EDGE,{"derivedFrom":sQuery(id+"F5.wireOp",EDGE,"E72.sketch_text.stroke-18")}),-1.0]])]});
            var Q1;
            Q1=makeQuery(id+"F5.imprint","IMPRINT",FACE,{"disambiguationData":[TD([[makeQuery(id+"F5.imprint","IMPRINT",EDGE,{"derivedFrom":sQuery(id+"F5.wireOp",EDGE,"E72.sketch_text.stroke-0")}),-1.0]])]});
            var Q2;
            Q2=makeQuery(id+"F5.imprint","IMPRINT",FACE,{"disambiguationData":[TD([[makeQuery(id+"F5.imprint","IMPRINT",EDGE,{"derivedFrom":sQuery(id+"F5.wireOp",EDGE,"E72.sketch_text.stroke-35")}),-1.0]])]});
            var Q3;
            Q3=makeQuery(id+"F5.imprint","IMPRINT",FACE,{"disambiguationData":[TD([[makeQuery(id+"F5.imprint","IMPRINT",EDGE,{"derivedFrom":sQuery(id+"F5.wireOp",EDGE,"E72.sketch_text.stroke-39")}),-1.0]])]});
            var Q4;
            Q4=makeQuery(id+"F5.imprint","IMPRINT",FACE,{"disambiguationData":[TD([[makeQuery(id+"F5.imprint","IMPRINT",EDGE,{"derivedFrom":sQuery(id+"F5.wireOp",EDGE,"E72.sketch_text.stroke-66")}),-1.0]])]});
            var Q5;
            Q5=makeQuery(id+"F5.imprint","IMPRINT",FACE,{"disambiguationData":[TD([[makeQuery(id+"F5.imprint","IMPRINT",EDGE,{"derivedFrom":sQuery(id+"F5.wireOp",EDGE,"E72.sketch_text.stroke-83")}),-1.0]])]});
            extrude(context, id + "F11", {"entities" : qUnion([Q0, Q1, Q2, Q3, Q4, Q5]), "operationType" : NewBodyOperationType.ADD, "depth" : 56 * mm, "hasSecondDirection" : true, "secondDirectionOppositeDirection" : false, "secondDirectionDepth" : 55 * mm});
        }
        {
            var Q0;
            Q0=makeQuery(id+"F5.imprint","IMPRINT",FACE,{"disambiguationData":[TD([[makeQuery(id+"F5.imprint","IMPRINT",EDGE,{"derivedFrom":sQuery(id+"F5.wireOp",EDGE,"E73.sketch_text.stroke-0")}),-1.0]])]});
            var Q1;
            Q1=makeQuery(id+"F5.imprint","IMPRINT",FACE,{"disambiguationData":[TD([[makeQuery(id+"F5.imprint","IMPRINT",EDGE,{"derivedFrom":sQuery(id+"F5.wireOp",EDGE,"E73.sketch_text.stroke-25")}),-1.0]])]});
            var Q2;
            Q2=makeQuery(id+"F5.imprint","IMPRINT",FACE,{"disambiguationData":[TD([[makeQuery(id+"F5.imprint","IMPRINT",EDGE,{"derivedFrom":sQuery(id+"F5.wireOp",EDGE,"E73.sketch_text.stroke-52")}),-1.0]])]});
            var Q3;
            Q3=makeQuery(id+"F5.imprint","IMPRINT",FACE,{"disambiguationData":[TD([[makeQuery(id+"F5.imprint","IMPRINT",EDGE,{"derivedFrom":sQuery(id+"F5.wireOp",EDGE,"E73.sketch_text.stroke-77")}),-1.0]])]});
            var Q4;
            Q4=makeQuery(id+"F5.imprint","IMPRINT",FACE,{"disambiguationData":[TD([[makeQuery(id+"F5.imprint","IMPRINT",EDGE,{"derivedFrom":sQuery(id+"F5.wireOp",EDGE,"E73.sketch_text.stroke-102")}),-1.0]])]});
            var Q5;
            Q5=makeQuery(id+"F5.imprint","IMPRINT",FACE,{"disambiguationData":[TD([[makeQuery(id+"F5.imprint","IMPRINT",EDGE,{"derivedFrom":sQuery(id+"F5.wireOp",EDGE,"E73.sketch_text.stroke-106")}),-1.0]])]});
            var Q6;
            Q6=makeQuery(id+"F5.imprint","IMPRINT",FACE,{"disambiguationData":[TD([[makeQuery(id+"F5.imprint","IMPRINT",EDGE,{"derivedFrom":sQuery(id+"F5.wireOp",EDGE,"E73.sketch_text.stroke-118")}),-1.0]])]});
            var Q7;
            Q7=makeQuery(id+"F5.imprint","IMPRINT",FACE,{"disambiguationData":[TD([[makeQuery(id+"F5.imprint","IMPRINT",EDGE,{"derivedFrom":sQuery(id+"F5.wireOp",EDGE,"E73.sketch_text.stroke-110")}),-1.0]])]});
            var Q8;
            Q8=makeQuery(id+"F5.imprint","IMPRINT",FACE,{"disambiguationData":[TD([[makeQuery(id+"F5.imprint","IMPRINT",EDGE,{"derivedFrom":sQuery(id+"F5.wireOp",EDGE,"E73.sketch_text.stroke-135")}),-1.0]])]});
            extrude(context, id + "F12", {"entities" : qUnion([Q0, Q1, Q2, Q3, Q4, Q5, Q6, Q7, Q8]), "operationType" : NewBodyOperationType.ADD, "depth" : 56 * mm, "hasSecondDirection" : true, "secondDirectionOppositeDirection" : false, "secondDirectionDepth" : 55 * mm});
        }
        {
            var Q0;
            {var subQ346=sQuery(id+"F0.wireOp",EDGE,"E1.2");var subQ354=sQuery(id+"F0.wireOp",EDGE,"E1.1");var subQ364=sQuery(id+"F0.wireOp",EDGE,"E1.3");var subQ377=sQuery(id+"F0.wireOp",EDGE,"E1.0");var subQ378=makeQuery(id+"F6.opExtrude","SWEPT_FACE",FACE,{"disambiguationData":[OSD([subQ377])]});Q0=makeQuery(id+"F12.boolean.opBoolean","SPLIT",FACE,{"disambiguationData":[TD([subQ378])],"derivedFrom":makeQuery(id+"F11.boolean.opBoolean","SPLIT",FACE,{"disambiguationData":[TD([subQ378])],"derivedFrom":makeQuery(id+"F10.boolean.opBoolean","SPLIT",FACE,{"disambiguationData":[TD([subQ378])],"derivedFrom":makeQuery(id+"F9.boolean.opBoolean","SPLIT",FACE,{"disambiguationData":[TD([subQ378])],"derivedFrom":makeQuery(id+"F6.opExtrude","CAP_FACE",FACE,{"disambiguationData":[OSD([subQ377,subQ354,subQ346,subQ364])],"isStart":false})})})})});}
            var sketch = newSketch(context, id + "F13", { "sketchPlane" : qUnion([Q0])});
            skLineSegment(sketch, "E74", {"start": v(12.55, 123) * mm, "end": v(12.55, 133.2) * mm});
            skLineSegment(sketch, "E75", {"start": v(12.55, 133.2) * mm, "end": v(25.55, 133.2) * mm});
            skLineSegment(sketch, "E76", {"start": v(25.55, 133.2) * mm, "end": v(25.55, 127.2) * mm, "construction": true});
            skArc(sketch, "E77", {"start": v(25.55, 133.2) * mm, "mid": v(28.55, 130.2) * mm, "end": v(25.55, 127.2) * mm});
            skLineSegment(sketch, "E78", {"start": v(25.55, 127.2) * mm, "end": v(17.55, 127.2) * mm});
            skLineSegment(sketch, "E79", {"start": v(17.55, 127.2) * mm, "end": v(17.55, 125.6) * mm});
            skLineSegment(sketch, "E80", {"start": v(17.55, 125.6) * mm, "end": v(28.55, 125.6) * mm});
            skLineSegment(sketch, "E81", {"start": v(14.15, 123) * mm, "end": v(14.15, 131.6) * mm});
            skLineSegment(sketch, "E82", {"start": v(14.15, 131.6) * mm, "end": v(25.55, 131.6) * mm});
            skLineSegment(sketch, "E83", {"start": v(25.55, 131.6) * mm, "end": v(25.55, 128.8) * mm});
            skLineSegment(sketch, "E84", {"start": v(25.55, 128.8) * mm, "end": v(17.55, 128.8) * mm});
            skLineSegment(sketch, "E85", {"start": v(17.55, 128.8) * mm, "end": v(17.55, 124) * mm, "construction": true});
            skPoint(sketch, "E86", {"position": v(17.55, 126.4) * mm});
            skArc(sketch, "E87", {"start": v(17.55, 128.8) * mm, "mid": v(15.15, 126.4) * mm, "end": v(17.55, 124) * mm});
            skLineSegment(sketch, "E88", {"start": v(17.55, 124) * mm, "end": v(28.55, 124) * mm});
            skPoint(sketch, "E89", {"position": v(28.55, 130.2) * mm});
            skSolve(sketch);
        }
        {
            var Q0;
            Q0=sQuery(id+"F13.wireOp",VERTEX,"E74.start");
            var Q1;
            Q1=qCreatedBy(makeId("Front.planeOp"),FACE);
            cPlane(context, id + "F14", {"entities" : qUnion([Q0, Q1]), "cplaneType" : CPlaneType.PLANE_POINT, "offset" : 25 * mm, "width" : 150 * mm, "height" : 150 * mm});
        }
        {
            var Q0;
            Q0=qCreatedBy(id+"F14.planeOp",FACE);
            var sketch = newSketch(context, id + "F15", { "sketchPlane" : qUnion([Q0])});
            skPoint(sketch, "E90.0", {"position": v(12.55, 55) * mm});
            skPoint(sketch, "E91.0", {"position": v(14.15, 55) * mm});
            skLineSegment(sketch, "E92.bottom", {"start": v(12.8, 55.25) * mm, "end": v(12.3, 55.25) * mm});
            skLineSegment(sketch, "E92.top", {"start": v(12.8, 54.75) * mm, "end": v(12.3, 54.75) * mm});
            skLineSegment(sketch, "E92.left", {"start": v(12.8, 55.25) * mm, "end": v(12.8, 54.75) * mm});
            skLineSegment(sketch, "E92.right", {"start": v(12.3, 55.25) * mm, "end": v(12.3, 54.75) * mm});
            skLineSegment(sketch, "E93.bottom", {"start": v(14.4, 55.25) * mm, "end": v(13.9, 55.25) * mm});
            skLineSegment(sketch, "E93.top", {"start": v(14.4, 54.75) * mm, "end": v(13.9, 54.75) * mm});
            skLineSegment(sketch, "E93.left", {"start": v(14.4, 55.25) * mm, "end": v(14.4, 54.75) * mm});
            skLineSegment(sketch, "E93.right", {"start": v(13.9, 55.25) * mm, "end": v(13.9, 54.75) * mm});
            skSolve(sketch);
        }
        {
            var Q0;
            Q0=makeQuery(id+"F15.imprint","IMPRINT",FACE,{"disambiguationData":[TD([[makeQuery(id+"F15.imprint","IMPRINT",EDGE,{"derivedFrom":sQuery(id+"F15.wireOp",EDGE,"E92.bottom")}),1.0]])]});
            var Q1;
            Q1=sQuery(id+"F13.wireOp",EDGE,"E74");
            var Q2;
            Q2=sQuery(id+"F13.wireOp",EDGE,"E75");
            var Q3;
            Q3=sQuery(id+"F13.wireOp",EDGE,"E77");
            var Q4;
            Q4=sQuery(id+"F13.wireOp",EDGE,"E78");
            var Q5;
            Q5=sQuery(id+"F13.wireOp",EDGE,"E79");
            var Q6;
            Q6=sQuery(id+"F13.wireOp",EDGE,"E80");
            sweep(context, id + "F16", {"operationType" : NewBodyOperationType.ADD, "profiles" : qUnion([Q0]), "path" : qUnion([Q1, Q2, Q3, Q4, Q5, Q6])});
        }
        {
            var Q0;
            Q0=makeQuery(id+"F15.imprint","IMPRINT",FACE,{"disambiguationData":[TD([[makeQuery(id+"F15.imprint","IMPRINT",EDGE,{"derivedFrom":sQuery(id+"F15.wireOp",EDGE,"E93.bottom")}),1.0]])]});
            var Q1;
            Q1=sQuery(id+"F13.wireOp",EDGE,"E81");
            var Q2;
            Q2=sQuery(id+"F13.wireOp",EDGE,"E82");
            var Q3;
            Q3=sQuery(id+"F13.wireOp",EDGE,"E83");
            var Q4;
            Q4=sQuery(id+"F13.wireOp",EDGE,"E87");
            var Q5;
            Q5=sQuery(id+"F13.wireOp",EDGE,"E88");
            var Q6;
            Q6=sQuery(id+"F13.wireOp",EDGE,"E84");
            sweep(context, id + "F17", {"operationType" : NewBodyOperationType.ADD, "profiles" : qUnion([Q0]), "path" : qUnion([Q1, Q2, Q3, Q4, Q5, Q6])});
        }
    });